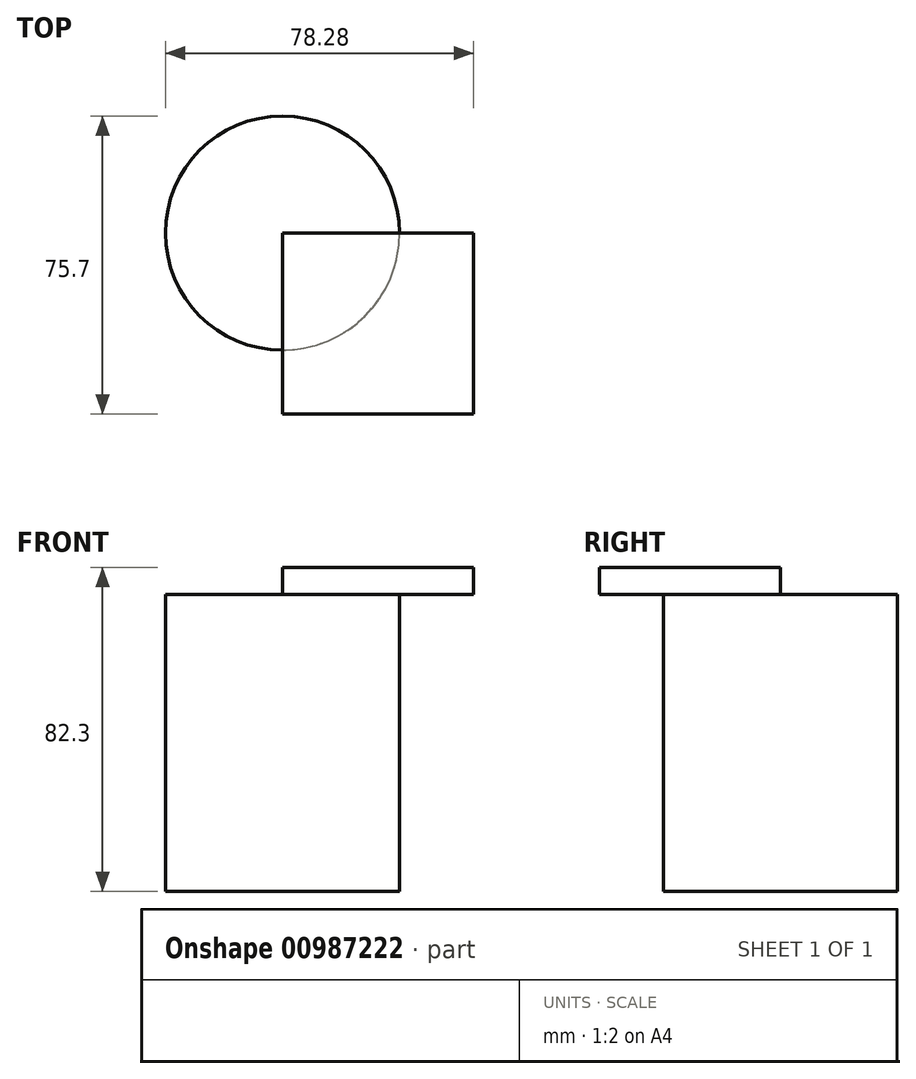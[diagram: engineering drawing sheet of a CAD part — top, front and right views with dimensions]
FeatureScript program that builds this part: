
annotation { "Feature Type Name" : "Feature", "Feature Type Description" : "" }
export const myFeature = defineFeature(function(context is Context, id is Id, definition is map)
    precondition{}
    {
        {
            var Q0;
            Q0=qCreatedBy(makeId("Top.planeOp"),FACE);
            var sketch = newSketch(context, id + "F0", { "sketchPlane" : qUnion([Q0])});
            skCircle(sketch, "E0", {"center": v(0, 0) * mm, "radius": 29.73 * mm});
            skSolve(sketch);
        }
        {
            var Q0;
            Q0 = qSketchRegion(id + "F0", true);
            extrude(context, id + "F1", {"entities" : qUnion([Q0]), "depth" : 75.44 * mm, "offsetDistance" : 25.4 * mm});
        }
        {
            var Q0;
            Q0=makeQuery(id+"F1.opExtrude","CAP_FACE",FACE,{"disambiguationData":[OSD([sQuery(id+"F0.wireOp",EDGE,"E0")])],"isStart":false});
            var sketch = newSketch(context, id + "F2", { "sketchPlane" : qUnion([Q0])});
            skLineSegment(sketch, "E1.bottom", {"start": v(0, 0) * mm, "end": v(48.55, 0) * mm});
            skLineSegment(sketch, "E1.top", {"start": v(0, -45.97) * mm, "end": v(48.55, -45.97) * mm});
            skLineSegment(sketch, "E1.left", {"start": v(0, 0) * mm, "end": v(0, -45.97) * mm});
            skLineSegment(sketch, "E1.right", {"start": v(48.55, 0) * mm, "end": v(48.55, -45.97) * mm});
            skSolve(sketch);
        }
        {
            var Q0;
            Q0 = qSketchRegion(id + "F2", true);
            extrude(context, id + "F3", {"entities" : qUnion([Q0]), "operationType" : NewBodyOperationType.ADD, "depth" : 6.86 * mm, "offsetDistance" : 25.4 * mm});
        }
    });
